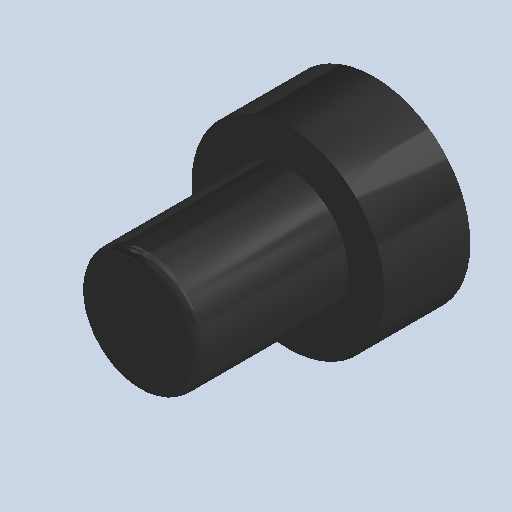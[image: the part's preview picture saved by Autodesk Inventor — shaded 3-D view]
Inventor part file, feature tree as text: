
AUTODESK INVENTOR PART (.ipt)
format: ipt  version: 2022.1 (Build 261234000, 234)  size: 92,672 bytes
history: mixed  units: mm (DEFAULTED — no unit token found)
features: other x8, fillet x1, imported_body x1
bodies: Body1 (imported_parasolid)
feature tree (10):
  other  "Sólido1"
  other  "Origen"
  other  "Plano YZ"
  other  "Plano XZ"
  other  "Plano XY"
  other  "Eje X"
  other  "Eje Y"
  other  "Eje Z"
  fillet  "Fillet1"  [1 undecoded]
  imported_body  NMx_Import_Brep_tag  [imported B-rep: ~6 faces, bbox_mm=[1.05, 0.0, 5.5]]
note: 1 required parameter value undecoded (feature->parameter linkage not recoverable at this tier; creation-order binding heuristic only, values carry confidence <= 0.55)
